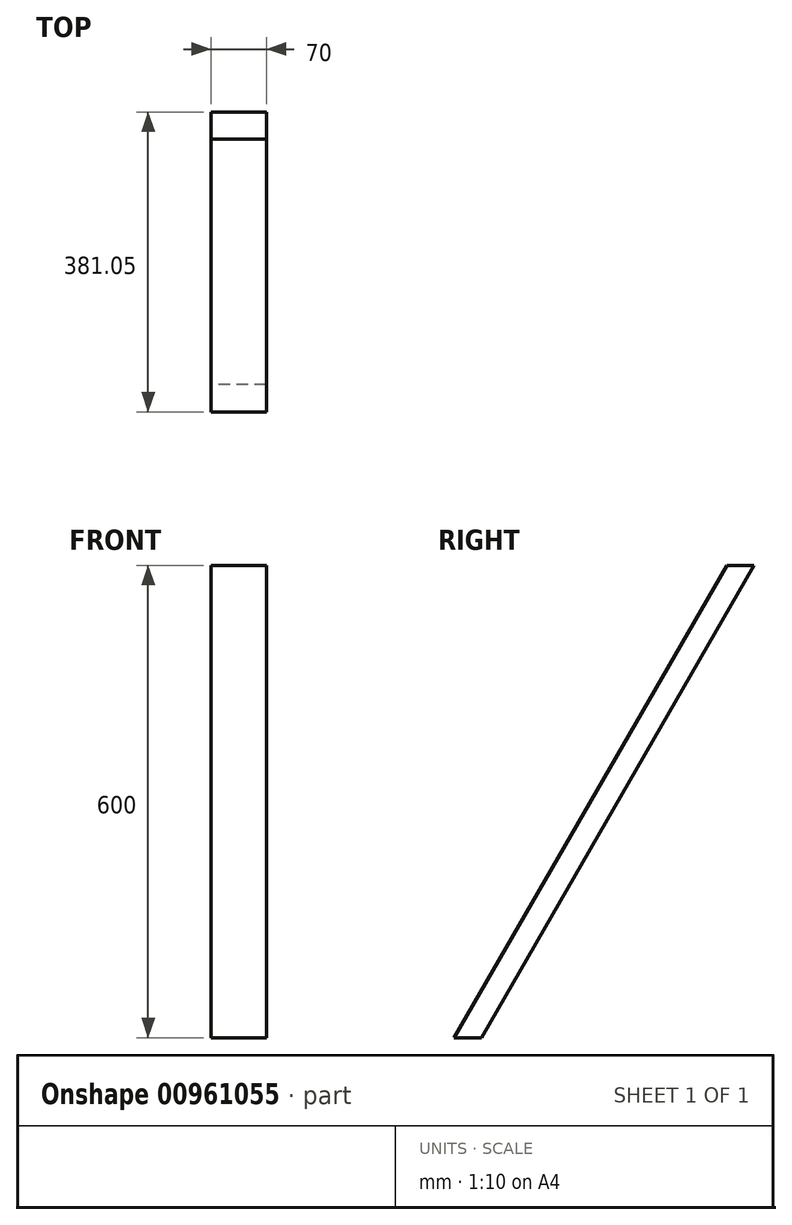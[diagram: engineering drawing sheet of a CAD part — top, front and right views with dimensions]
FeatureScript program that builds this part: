
annotation { "Feature Type Name" : "Feature", "Feature Type Description" : "" }
export const myFeature = defineFeature(function(context is Context, id is Id, definition is map)
    precondition{}
    {
        {
            var Q0;
            Q0=qCreatedBy(makeId("Right.planeOp"),FACE);
            var sketch = newSketch(context, id + "F0", { "sketchPlane" : qUnion([Q0])});
            skLineSegment(sketch, "E0", {"start": v(-166.97, 5.63) * mm, "end": v(-513.38, -594.37) * mm});
            skLineSegment(sketch, "E1.0", {"start": v(-201.61, 5.63) * mm, "end": v(-548.02, -594.37) * mm});
            skLineSegment(sketch, "E2", {"start": v(-548.02, -594.37) * mm, "end": v(-513.38, -594.37) * mm});
            skLineSegment(sketch, "E3", {"start": v(-201.61, 5.63) * mm, "end": v(-166.97, 5.63) * mm});
            skSolve(sketch);
        }
        {
            var Q0;
            Q0=makeQuery(id+"F0.imprint","IMPRINT",FACE,{"disambiguationData":[TD([[makeQuery(id+"F0.imprint","IMPRINT",EDGE,{"derivedFrom":sQuery(id+"F0.wireOp",EDGE,"E0")}),-1.0]])]});
            extrude(context, id + "F1", {"entities" : qUnion([Q0]), "endBound" : BoundingType.SYMMETRIC, "depth" : 70 * mm, "offsetDistance" : 25 * mm});
        }
    });
